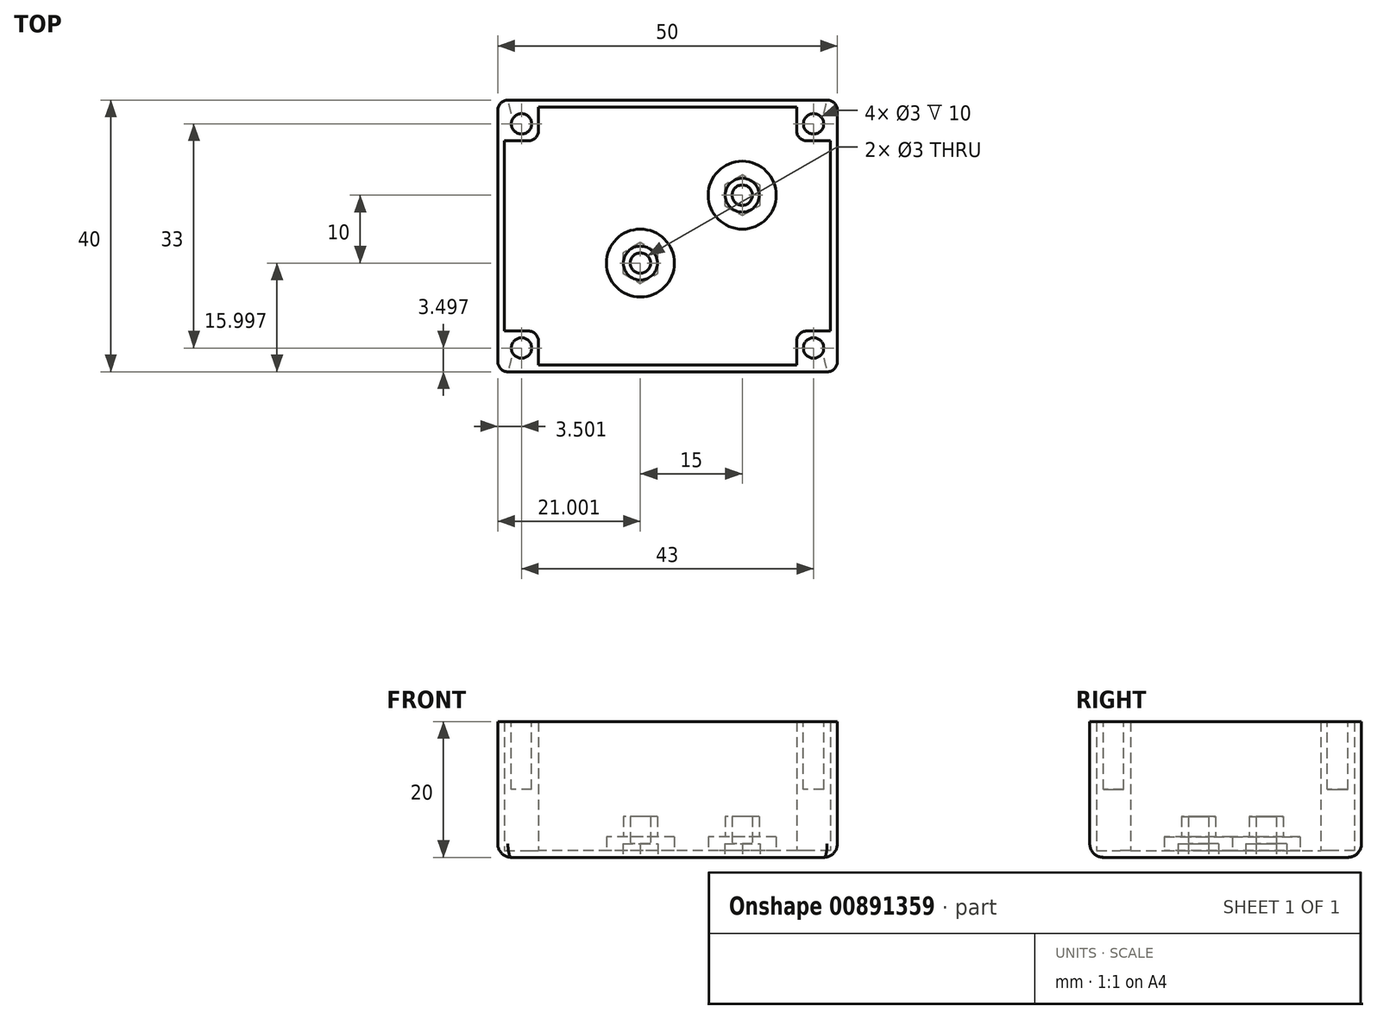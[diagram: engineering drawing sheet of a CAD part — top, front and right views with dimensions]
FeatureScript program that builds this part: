
annotation { "Feature Type Name" : "Feature", "Feature Type Description" : "" }
export const myFeature = defineFeature(function(context is Context, id is Id, definition is map)
    precondition{}
    {
        {
            var Q0;
            Q0=qCreatedBy(makeId("Top.planeOp"),FACE);
            var sketch = newSketch(context, id + "F0", { "sketchPlane" : qUnion([Q0])});
            skLineSegment(sketch, "E0.bottom", {"start": v(-59.42, 55.28) * mm, "end": v(-9.42, 55.28) * mm});
            skLineSegment(sketch, "E0.top", {"start": v(-59.42, 15.28) * mm, "end": v(-9.42, 15.28) * mm});
            skLineSegment(sketch, "E0.left", {"start": v(-59.42, 55.28) * mm, "end": v(-59.42, 15.28) * mm});
            skLineSegment(sketch, "E0.right", {"start": v(-9.42, 55.28) * mm, "end": v(-9.42, 15.28) * mm});
            skSolve(sketch);
        }
        {
            var Q0;
            Q0=makeQuery(id+"F0.imprint","IMPRINT",FACE,{"disambiguationData":[TD([[makeQuery(id+"F0.imprint","IMPRINT",EDGE,{"derivedFrom":sQuery(id+"F0.wireOp",EDGE,"E0.bottom")}),-1.0]])]});
            var Q1;
            Q1 = qSketchRegion(id + "F2", true);
            extrude(context, id + "F1", {"entities" : qUnion([Q0, Q1]), "depth" : 20 * mm, "offsetDistance" : 25 * mm});
        }
        {
            var Q0;
            Q0=makeQuery(id+"F1.opExtrude","CAP_FACE",FACE,{"disambiguationData":[OSD([sQuery(id+"F0.wireOp",EDGE,"E0.bottom"),sQuery(id+"F0.wireOp",EDGE,"E0.top"),sQuery(id+"F0.wireOp",EDGE,"E0.left"),sQuery(id+"F0.wireOp",EDGE,"E0.right")])],"isStart":false});
            var sketch = newSketch(context, id + "F2", { "sketchPlane" : qUnion([Q0])});
            skLineSegment(sketch, "E1.bottom", {"start": v(-10.42, 16.28) * mm, "end": v(-58.42, 16.28) * mm});
            skLineSegment(sketch, "E1.top", {"start": v(-10.42, 54.28) * mm, "end": v(-58.42, 54.28) * mm});
            skLineSegment(sketch, "E1.left", {"start": v(-10.42, 16.28) * mm, "end": v(-10.42, 54.28) * mm});
            skLineSegment(sketch, "E1.right", {"start": v(-58.42, 16.28) * mm, "end": v(-58.42, 54.28) * mm});
            skPoint(sketch, "E1.middle", {"position": v(-34.42, 35.28) * mm});
            skPoint(sketch, "E1.middle.positionSnap0", {"position": v(-59.42, 35.28) * mm});
            skPoint(sketch, "E1.middle.positionSnap1", {"position": v(-34.42, 55.28) * mm});
            skPoint(sketch, "E1.centerSnap0", {"position": v(-59.42, 35.28) * mm});
            skPoint(sketch, "E1.centerSnap1", {"position": v(-34.42, 55.28) * mm});
            skSolve(sketch);
        }
        {
            var Q0;
            Q0=makeQuery(id+"F2.imprint","IMPRINT",FACE,{"disambiguationData":[TD([[makeQuery(id+"F2.imprint","IMPRINT",EDGE,{"derivedFrom":sQuery(id+"F2.wireOp",EDGE,"E1.bottom")}),-1.0]])]});
            extrude(context, id + "F3", {"entities" : qUnion([Q0]), "operationType" : NewBodyOperationType.REMOVE, "oppositeDirection" : true, "depth" : 19 * mm, "offsetDistance" : 25 * mm});
        }
        {
            var Q0;
            Q0=makeQuery(id+"F3.boolean.opBoolean","COPY",FACE,{"derivedFrom":makeQuery(id+"F3.opExtrude","CAP_FACE",FACE,{"disambiguationData":[OSD([sQuery(id+"F2.wireOp",EDGE,"E1.bottom"),sQuery(id+"F2.wireOp",EDGE,"E1.top"),sQuery(id+"F2.wireOp",EDGE,"E1.left"),sQuery(id+"F2.wireOp",EDGE,"E1.right")])],"isStart":false})});
            var sketch = newSketch(context, id + "F4", { "sketchPlane" : qUnion([Q0])});
            skLineSegment(sketch, "E2.bottom", {"start": v(-58.42, 54.28) * mm, "end": v(-53.42, 54.28) * mm});
            skLineSegment(sketch, "E2.top", {"start": v(-58.42, 49.28) * mm, "end": v(-53.42, 49.28) * mm});
            skLineSegment(sketch, "E2.left", {"start": v(-58.42, 54.28) * mm, "end": v(-58.42, 49.28) * mm});
            skLineSegment(sketch, "E2.right", {"start": v(-53.42, 54.28) * mm, "end": v(-53.42, 49.28) * mm});
            skLineSegment(sketch, "E3.bottom", {"start": v(-10.42, 54.28) * mm, "end": v(-15.42, 54.28) * mm});
            skLineSegment(sketch, "E3.top", {"start": v(-10.42, 49.28) * mm, "end": v(-15.42, 49.28) * mm});
            skLineSegment(sketch, "E3.left", {"start": v(-10.42, 54.28) * mm, "end": v(-10.42, 49.28) * mm});
            skLineSegment(sketch, "E3.right", {"start": v(-15.42, 54.28) * mm, "end": v(-15.42, 49.28) * mm});
            skLineSegment(sketch, "E4.bottom", {"start": v(-58.42, 16.28) * mm, "end": v(-53.42, 16.28) * mm});
            skLineSegment(sketch, "E4.top", {"start": v(-58.42, 21.28) * mm, "end": v(-53.42, 21.28) * mm});
            skLineSegment(sketch, "E4.left", {"start": v(-58.42, 16.28) * mm, "end": v(-58.42, 21.28) * mm});
            skLineSegment(sketch, "E4.right", {"start": v(-53.42, 16.28) * mm, "end": v(-53.42, 21.28) * mm});
            skLineSegment(sketch, "E5.bottom", {"start": v(-10.42, 16.28) * mm, "end": v(-15.42, 16.28) * mm});
            skLineSegment(sketch, "E5.top", {"start": v(-10.42, 21.28) * mm, "end": v(-15.42, 21.28) * mm});
            skLineSegment(sketch, "E5.left", {"start": v(-10.42, 16.28) * mm, "end": v(-10.42, 21.28) * mm});
            skLineSegment(sketch, "E5.right", {"start": v(-15.42, 16.28) * mm, "end": v(-15.42, 21.28) * mm});
            skSolve(sketch);
        }
        {
            var Q0;
            Q0=makeQuery(id+"F4.imprint","IMPRINT",FACE,{"disambiguationData":[TD([[makeQuery(id+"F4.imprint","IMPRINT",EDGE,{"derivedFrom":sQuery(id+"F4.wireOp",EDGE,"E2.bottom")}),1.0]])]});
            var Q1;
            Q1=makeQuery(id+"F4.imprint","IMPRINT",FACE,{"disambiguationData":[TD([[makeQuery(id+"F4.imprint","IMPRINT",EDGE,{"derivedFrom":sQuery(id+"F4.wireOp",EDGE,"E3.bottom")}),1.0]])]});
            var Q2;
            Q2=makeQuery(id+"F4.imprint","IMPRINT",FACE,{"disambiguationData":[TD([[makeQuery(id+"F4.imprint","IMPRINT",EDGE,{"derivedFrom":sQuery(id+"F4.wireOp",EDGE,"E4.bottom")}),-1.0]])]});
            var Q3;
            Q3=makeQuery(id+"F4.imprint","IMPRINT",FACE,{"disambiguationData":[TD([[makeQuery(id+"F4.imprint","IMPRINT",EDGE,{"derivedFrom":sQuery(id+"F4.wireOp",EDGE,"E5.bottom")}),-1.0]])]});
            extrude(context, id + "F5", {"entities" : qUnion([Q0, Q1, Q2, Q3]), "operationType" : NewBodyOperationType.ADD, "depth" : 19 * mm, "offsetDistance" : 25 * mm});
        }
        {
            var Q0;
            Q0=makeQuery(id+"F5.boolean.opBoolean","MERGE",FACE,{"derivedFrom":[makeQuery(id+"F1.opExtrude","CAP_FACE",FACE,{"disambiguationData":[OSD([sQuery(id+"F0.wireOp",EDGE,"E0.bottom"),sQuery(id+"F0.wireOp",EDGE,"E0.top"),sQuery(id+"F0.wireOp",EDGE,"E0.left"),sQuery(id+"F0.wireOp",EDGE,"E0.right")])],"isStart":false}),makeQuery(id+"F5.opExtrude","CAP_FACE",FACE,{"disambiguationData":[OSD([sQuery(id+"F4.wireOp",EDGE,"E2.bottom"),sQuery(id+"F4.wireOp",EDGE,"E2.top"),sQuery(id+"F4.wireOp",EDGE,"E2.left"),sQuery(id+"F4.wireOp",EDGE,"E2.right")])],"isStart":false}),makeQuery(id+"F5.opExtrude","CAP_FACE",FACE,{"disambiguationData":[OSD([sQuery(id+"F4.wireOp",EDGE,"E3.bottom"),sQuery(id+"F4.wireOp",EDGE,"E3.top"),sQuery(id+"F4.wireOp",EDGE,"E3.left"),sQuery(id+"F4.wireOp",EDGE,"E3.right")])],"isStart":false}),makeQuery(id+"F5.opExtrude","CAP_FACE",FACE,{"disambiguationData":[OSD([sQuery(id+"F4.wireOp",EDGE,"E4.bottom"),sQuery(id+"F4.wireOp",EDGE,"E4.top"),sQuery(id+"F4.wireOp",EDGE,"E4.left"),sQuery(id+"F4.wireOp",EDGE,"E4.right")])],"isStart":false}),makeQuery(id+"F5.opExtrude","CAP_FACE",FACE,{"disambiguationData":[OSD([sQuery(id+"F4.wireOp",EDGE,"E5.bottom"),sQuery(id+"F4.wireOp",EDGE,"E5.top"),sQuery(id+"F4.wireOp",EDGE,"E5.left"),sQuery(id+"F4.wireOp",EDGE,"E5.right")])],"isStart":false})]});
            var sketch = newSketch(context, id + "F6", { "sketchPlane" : qUnion([Q0])});
            skCircle(sketch, "E6", {"center": v(-55.92, 51.78) * mm, "radius": 1.5 * mm});
            skPoint(sketch, "E6.centerSnap0", {"position": v(-53.42, 51.78) * mm});
            skPoint(sketch, "E6.centerSnap1", {"position": v(-55.92, 49.28) * mm});
            skCircle(sketch, "E7", {"center": v(-12.92, 51.78) * mm, "radius": 1.5 * mm});
            skPoint(sketch, "E7.centerSnap0", {"position": v(-12.92, 49.28) * mm});
            skCircle(sketch, "E8", {"center": v(-55.92, 18.78) * mm, "radius": 1.5 * mm});
            skPoint(sketch, "E8.centerSnap0", {"position": v(-53.42, 18.78) * mm});
            skCircle(sketch, "E9", {"center": v(-12.92, 18.78) * mm, "radius": 1.5 * mm});
            skPoint(sketch, "E9.centerSnap0", {"position": v(-15.42, 18.78) * mm});
            skPoint(sketch, "E9.centerSnap1", {"position": v(-12.92, 21.28) * mm});
            skSolve(sketch);
        }
        {
            var Q0;
            Q0=makeQuery(id+"F6.imprint","IMPRINT",FACE,{"disambiguationData":[TD([[makeQuery(id+"F6.imprint","IMPRINT",EDGE,{"derivedFrom":sQuery(id+"F6.wireOp",EDGE,"E6")}),1.0]])]});
            var Q1;
            Q1=makeQuery(id+"F6.imprint","IMPRINT",FACE,{"disambiguationData":[TD([[makeQuery(id+"F6.imprint","IMPRINT",EDGE,{"derivedFrom":sQuery(id+"F6.wireOp",EDGE,"E8")}),1.0]])]});
            var Q2;
            Q2=makeQuery(id+"F6.imprint","IMPRINT",FACE,{"disambiguationData":[TD([[makeQuery(id+"F6.imprint","IMPRINT",EDGE,{"derivedFrom":sQuery(id+"F6.wireOp",EDGE,"E9")}),1.0]])]});
            var Q3;
            Q3=makeQuery(id+"F6.imprint","IMPRINT",FACE,{"disambiguationData":[TD([[makeQuery(id+"F6.imprint","IMPRINT",EDGE,{"derivedFrom":sQuery(id+"F6.wireOp",EDGE,"E7")}),1.0]])]});
            extrude(context, id + "F7", {"entities" : qUnion([Q0, Q1, Q2, Q3]), "operationType" : NewBodyOperationType.REMOVE, "oppositeDirection" : true, "depth" : 10 * mm, "offsetDistance" : 25 * mm});
        }
        {
            var Q0;
            Q0=makeQuery(id+"F3.boolean.opBoolean","COPY",FACE,{"derivedFrom":makeQuery(id+"F3.opExtrude","CAP_FACE",FACE,{"disambiguationData":[OSD([sQuery(id+"F2.wireOp",EDGE,"E1.bottom"),sQuery(id+"F2.wireOp",EDGE,"E1.top"),sQuery(id+"F2.wireOp",EDGE,"E1.left"),sQuery(id+"F2.wireOp",EDGE,"E1.right")])],"isStart":false})});
            var sketch = newSketch(context, id + "F8", { "sketchPlane" : qUnion([Q0])});
            skCircle(sketch, "E10", {"center": v(-23.42, 41.28) * mm, "radius": 2.5 * mm});
            skCircle(sketch, "E11", {"center": v(-23.42, 41.28) * mm, "radius": 1.5 * mm});
            skCircle(sketch, "E12", {"center": v(-38.42, 31.28) * mm, "radius": 2.5 * mm});
            skCircle(sketch, "E13", {"center": v(-38.42, 31.28) * mm, "radius": 1.5 * mm});
            skSolve(sketch);
        }
        {
            var Q0;
            Q0=makeQuery(id+"F8.imprint","IMPRINT",FACE,{"disambiguationData":[TD([[makeQuery(id+"F8.imprint","IMPRINT",EDGE,{"derivedFrom":sQuery(id+"F8.wireOp",EDGE,"E12")}),1.0]])]});
            var Q1;
            Q1=makeQuery(id+"F8.imprint","IMPRINT",FACE,{"disambiguationData":[TD([[makeQuery(id+"F8.imprint","IMPRINT",EDGE,{"derivedFrom":sQuery(id+"F8.wireOp",EDGE,"E10")}),1.0]])]});
            extrude(context, id + "F9", {"entities" : qUnion([Q0, Q1]), "operationType" : NewBodyOperationType.ADD, "depth" : 5 * mm, "offsetDistance" : 25 * mm});
        }
        {
            var Q0;
            Q0=makeQuery(id+"F9.boolean.opBoolean","SPLIT",FACE,{"disambiguationData":[TD([makeQuery(id+"F9.opExtrude","SWEPT_FACE",FACE,{"disambiguationData":[OSD([sQuery(id+"F8.wireOp",EDGE,"E13")])]})])],"derivedFrom":makeQuery(id+"F3.boolean.opBoolean","COPY",FACE,{"derivedFrom":makeQuery(id+"F3.opExtrude","CAP_FACE",FACE,{"disambiguationData":[OSD([sQuery(id+"F2.wireOp",EDGE,"E1.bottom"),sQuery(id+"F2.wireOp",EDGE,"E1.top"),sQuery(id+"F2.wireOp",EDGE,"E1.left"),sQuery(id+"F2.wireOp",EDGE,"E1.right")])],"isStart":false})})});
            var Q1;
            Q1=makeQuery(id+"F9.boolean.opBoolean","SPLIT",FACE,{"disambiguationData":[TD([makeQuery(id+"F9.opExtrude","SWEPT_FACE",FACE,{"disambiguationData":[OSD([sQuery(id+"F8.wireOp",EDGE,"E11")])]})])],"derivedFrom":makeQuery(id+"F3.boolean.opBoolean","COPY",FACE,{"derivedFrom":makeQuery(id+"F3.opExtrude","CAP_FACE",FACE,{"disambiguationData":[OSD([sQuery(id+"F2.wireOp",EDGE,"E1.bottom"),sQuery(id+"F2.wireOp",EDGE,"E1.top"),sQuery(id+"F2.wireOp",EDGE,"E1.left"),sQuery(id+"F2.wireOp",EDGE,"E1.right")])],"isStart":false})})});
            extrude(context, id + "F10", {"entities" : qUnion([Q0, Q1]), "operationType" : NewBodyOperationType.REMOVE, "oppositeDirection" : true, "depth" : 2 * mm, "offsetDistance" : 25 * mm});
        }
        {
            var Q0;
            {var subQ0=sQuery(id+"F2.wireOp",EDGE,"E1.bottom");var subQ1=sQuery(id+"F2.wireOp",EDGE,"E1.top");var subQ2=sQuery(id+"F2.wireOp",EDGE,"E1.left");var subQ3=sQuery(id+"F2.wireOp",EDGE,"E1.right");Q0=makeQuery(id+"F9.boolean.opBoolean","SPLIT",FACE,{"disambiguationData":[TD([makeQuery(id+"F3.boolean.opBoolean","COPY",FACE,{"derivedFrom":makeQuery(id+"F3.opExtrude","SWEPT_FACE",FACE,{"disambiguationData":[OSD([subQ0])]})})])],"derivedFrom":makeQuery(id+"F3.boolean.opBoolean","COPY",FACE,{"derivedFrom":makeQuery(id+"F3.opExtrude","CAP_FACE",FACE,{"disambiguationData":[OSD([subQ0,subQ1,subQ2,subQ3])],"isStart":false})})});}
            var sketch = newSketch(context, id + "F11", { "sketchPlane" : qUnion([Q0])});
            skCircle(sketch, "E14", {"center": v(-38.42, 31.28) * mm, "radius": 5 * mm});
            skCircle(sketch, "E15", {"center": v(-23.42, 41.28) * mm, "radius": 5 * mm});
            skSolve(sketch);
        }
        {
            var Q0;
            Q0=makeQuery(id+"F11.imprint","IMPRINT",FACE,{"disambiguationData":[TD([[makeQuery(id+"F11.imprint","IMPRINT",EDGE,{"derivedFrom":sQuery(id+"F11.wireOp",EDGE,"E14")}),1.0]])]});
            var Q1;
            Q1=makeQuery(id+"F11.imprint","IMPRINT",FACE,{"disambiguationData":[TD([[makeQuery(id+"F11.imprint","IMPRINT",EDGE,{"derivedFrom":sQuery(id+"F11.wireOp",EDGE,"E15")}),1.0]])]});
            extrude(context, id + "F12", {"entities" : qUnion([Q0, Q1]), "operationType" : NewBodyOperationType.ADD, "depth" : 2 * mm, "offsetDistance" : 25 * mm});
        }
        {
            var Q0;
            Q0=makeQuery(id+"F1.opExtrude","CAP_FACE",FACE,{"disambiguationData":[OSD([sQuery(id+"F0.wireOp",EDGE,"E0.bottom"),sQuery(id+"F0.wireOp",EDGE,"E0.top"),sQuery(id+"F0.wireOp",EDGE,"E0.left"),sQuery(id+"F0.wireOp",EDGE,"E0.right")])],"isStart":true});
            var sketch = newSketch(context, id + "F13", { "sketchPlane" : qUnion([Q0])});
            skCircle(sketch, "E16", {"center": v(-38.42, -31.28) * mm, "radius": 3 * mm});
            skCircle(sketch, "E17", {"center": v(-23.42, -41.28) * mm, "radius": 3 * mm});
            skCircle(sketch, "E18.cCircle", {"center": v(-38.42, -31.28) * mm, "radius": 3 * mm, "construction": true});
            skLineSegment(sketch, "E18.0", {"start": v(-38.42, -28.28) * mm, "end": v(-35.82, -29.78) * mm});
            skLineSegment(sketch, "E18.1", {"start": v(-35.82, -29.78) * mm, "end": v(-35.82, -32.78) * mm});
            skLineSegment(sketch, "E18.2", {"start": v(-35.82, -32.78) * mm, "end": v(-38.42, -34.28) * mm});
            skLineSegment(sketch, "E18.3", {"start": v(-38.42, -34.28) * mm, "end": v(-41.02, -32.78) * mm});
            skLineSegment(sketch, "E18.4", {"start": v(-41.02, -32.78) * mm, "end": v(-41.02, -29.78) * mm});
            skLineSegment(sketch, "E18.5", {"start": v(-41.02, -29.78) * mm, "end": v(-38.42, -28.28) * mm});
            skCircle(sketch, "E19.cCircle", {"center": v(-23.42, -41.28) * mm, "radius": 3 * mm, "construction": true});
            skLineSegment(sketch, "E19.0", {"start": v(-23.42, -38.28) * mm, "end": v(-20.82, -39.78) * mm});
            skLineSegment(sketch, "E19.1", {"start": v(-20.82, -39.78) * mm, "end": v(-20.82, -42.78) * mm});
            skLineSegment(sketch, "E19.2", {"start": v(-20.82, -42.78) * mm, "end": v(-23.42, -44.28) * mm});
            skLineSegment(sketch, "E19.3", {"start": v(-23.42, -44.28) * mm, "end": v(-26.02, -42.78) * mm});
            skLineSegment(sketch, "E19.4", {"start": v(-26.02, -42.78) * mm, "end": v(-26.02, -39.78) * mm});
            skLineSegment(sketch, "E19.5", {"start": v(-26.02, -39.78) * mm, "end": v(-23.42, -38.28) * mm});
            skSolve(sketch);
        }
        {
            var Q0;
            Q0=makeQuery(id+"F13.imprint","IMPRINT",FACE,{"disambiguationData":[TD([[makeQuery(id+"F13.imprint","IMPRINT",EDGE,{"derivedFrom":sQuery(id+"F13.wireOp",EDGE,"E18.0")}),-1.0]])]});
            var Q1;
            Q1=makeQuery(id+"F13.imprint","IMPRINT",FACE,{"disambiguationData":[TD([[makeQuery(id+"F13.imprint","IMPRINT",EDGE,{"derivedFrom":sQuery(id+"F13.wireOp",EDGE,"E19.0")}),-1.0]])]});
            extrude(context, id + "F14", {"entities" : qUnion([Q0, Q1]), "operationType" : NewBodyOperationType.REMOVE, "oppositeDirection" : true, "depth" : 2 * mm, "offsetDistance" : 25 * mm});
        }
        {
            var Q0;
            Q0=makeQuery(id+"F1.opExtrude","SWEPT_EDGE",EDGE,{"disambiguationData":[OSD([sQuery(id+"F0.wireOp",EDGE,"E0.top"),sQuery(id+"F0.wireOp",EDGE,"E0.left")])]});
            var Q1;
            Q1=makeQuery(id+"F1.opExtrude","SWEPT_EDGE",EDGE,{"disambiguationData":[OSD([sQuery(id+"F0.wireOp",EDGE,"E0.top"),sQuery(id+"F0.wireOp",EDGE,"E0.right")])]});
            var Q2;
            Q2=makeQuery(id+"F1.opExtrude","SWEPT_EDGE",EDGE,{"disambiguationData":[OSD([sQuery(id+"F0.wireOp",EDGE,"E0.bottom"),sQuery(id+"F0.wireOp",EDGE,"E0.right")])]});
            var Q3;
            Q3=makeQuery(id+"F1.opExtrude","SWEPT_EDGE",EDGE,{"disambiguationData":[OSD([sQuery(id+"F0.wireOp",EDGE,"E0.bottom"),sQuery(id+"F0.wireOp",EDGE,"E0.left")])]});
            var Q4;
            Q4=makeQuery(id+"F5.opExtrude","SWEPT_EDGE",EDGE,{"disambiguationData":[OSD([sQuery(id+"F4.wireOp",EDGE,"E2.top"),sQuery(id+"F4.wireOp",EDGE,"E2.right")])]});
            var Q5;
            Q5=makeQuery(id+"F5.opExtrude","SWEPT_EDGE",EDGE,{"disambiguationData":[OSD([sQuery(id+"F4.wireOp",EDGE,"E3.top"),sQuery(id+"F4.wireOp",EDGE,"E3.right")])]});
            var Q6;
            Q6=makeQuery(id+"F5.opExtrude","SWEPT_EDGE",EDGE,{"disambiguationData":[OSD([sQuery(id+"F4.wireOp",EDGE,"E5.top"),sQuery(id+"F4.wireOp",EDGE,"E5.right")])]});
            var Q7;
            Q7=makeQuery(id+"F5.opExtrude","SWEPT_EDGE",EDGE,{"disambiguationData":[OSD([sQuery(id+"F4.wireOp",EDGE,"E4.top"),sQuery(id+"F4.wireOp",EDGE,"E4.right")])]});
            fillet(context, id + "F15", {"entities" : qUnion([Q0, Q1, Q2, Q3, Q4, Q5, Q6, Q7]), "radius" : 1.5 * mm, "tangentPropagation" : true, "allowEdgeOverflow" : false});
        }
        {
            var Q0;
            Q0=makeQuery(id+"F1.opExtrude","CAP_EDGE",EDGE,{"disambiguationData":[OSD([sQuery(id+"F0.wireOp",EDGE,"E0.left")])],"isStart":true});
            fillet(context, id + "F16", {"entities" : qUnion([Q0]), "radius" : 2 * mm, "tangentPropagation" : true, "allowEdgeOverflow" : false});
        }
    });
